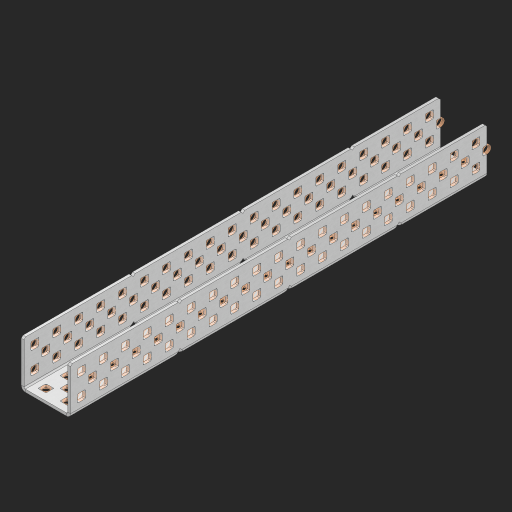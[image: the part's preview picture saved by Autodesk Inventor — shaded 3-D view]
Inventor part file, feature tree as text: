
AUTODESK INVENTOR PART (.ipt)
format: ipt  version: 2023 (Build 270158000, 158)  size: 2,187,264 bytes
history: native  units: in
note: dims shown in document units (in); Inventor stores cm internally (conversion verified against a paired STEP export)
features: other x234, extrude x226, sheet_metal_op x8, sketch x7, mirror x3, pattern_linear x2, chamfer x1
ambient origin geometry x8: Origin, YZ Plane, XZ Plane, XY Plane, X Axis, Y Axis, Z Axis, Center Point
bodies: Solid1 (feature_tree), Body (feature_tree)
feature tree (481):
  sheet_metal_op  "Flanges"
  sheet_metal_op  "Body Pattern"
  pattern_linear  "Center Pattern"  Spacing1=1.0in  [1 undecoded]
  other  "Arc Length"
  mirror  "Notch Mirror"
  pattern_linear  "Notch Pattern"  Spacing1=0.25in  [1 undecoded]
  other  "Diagonal Plane"
  mirror  "Flange 1"
  mirror  "Flange 2"
  chamfer  "End Chamfer"
  sketch  "Sketch1"  dims[d0=1.0in]
  other  "Plate1"
  sketch  "Sketch2"  dims[d1=9.5in]
  other  "Plate2"
  sheet_metal_op  "Bend1"
  sheet_metal_op  "Corner1"
  sketch  "Sketch8"  dims[d2=0.0625in]
  sketch  "Sketch9"  dims[d3=0.0625in]
  other  "Srf91"
  sheet_metal_op  "Body Pattern Sketch"
  other  "Srf92"
  sketch  "Sketch13"  dims[d4=0.0312in]
  sketch  "Sketch15"  dims[d5=0.125in]
  sketch  "Sketch16"  dims[d6=0.0625in d7=1.0in d8=90.0deg d9=0.0312in d10=0.25in d11=0.0625in d12=0.0625in d49=0.182in d50=0.02in d52=0.25in d53=0.0625in d54=0.0in d55=0.172in d56=1.0in d57=0.0in d60=7.4803in d62=0.5in d63=0.7874in d65=0.5in d85=0.1473in d86=0.1782in d88=0.04in d89=0.0625in d90=0.0in d91=0.04in d92=0.0491in d95=2.5in d96=0.04in d97=0.25in d98=45.0deg d99=0.25in d102=2.497in d106=0.182in d107=0.02in d108=0.5in d110=0.0625in d111=0.0in d112=0.172in d113=0.5in d114=0.0in d117=0.5in d118=0.5in d131=0.25in d132=0.25in]
  other  "Srf786"
  other  "Srf889"
  other  "Srf890"
  other  "Srf891"
  other  "Srf892"
  other  "Srf893"
  other  "Srf894"
  other  "Srf895"
  other  "Srf896"
  other  "Srf996"
  other  "Srf997"
  other  "Srf998"
  other  "Srf999"
  other  "Srf1000"
  other  "Srf1255"
  other  "Srf1256"
  other  "Srf1257"
  other  "Srf1258"
  other  "Srf1259"
  other  "Srf1315"
  other  "Srf1316"
  other  "Srf1317"
  other  "Srf1325"
  other  "Srf1326"
  other  "Srf1327"
  other  "Srf1328"
  other  "Srf1329"
  other  "Srf1330"
  other  "Srf1331"
  other  "Srf1332"
  other  "Srf1338"
  other  "Srf1339"
  other  "Srf1340"
  other  "Srf1341"
  other  "Srf1342"
  other  "Srf1369"
  other  "Srf1370"
  other  "Srf1371"
  other  "Srf1372"
  other  "Srf1373"
  other  "Srf1374"
  other  "Srf1375"
  other  "Srf1376"
  other  "Srf1384"
  other  "Srf1385"
  other  "Srf1386"
  other  "Srf1387"
  other  "Srf1388"
  other  "Srf1389"
  other  "Srf1390"
  other  "Srf1391"
  other  "Srf1397"
  other  "Srf1398"
  other  "Srf1399"
  other  "Srf1400"
  other  "Srf1401"
  other  "Srf1428"
  other  "Srf1429"
  other  "Srf1430"
  other  "Srf1431"
  other  "Srf1432"
  other  "Srf1433"
  other  "Srf1434"
  other  "Srf1473"
  other  "Srf1474"
  other  "Srf1475"
  other  "Srf1476"
  other  "Srf1477"
  other  "Srf1478"
  other  "Srf1479"
  other  "Srf1480"
  other  "Srf1481"
  other  "Srf1482"
  other  "Srf1483"
  other  "Srf1484"
  other  "Srf1485"
  other  "Srf1486"
  other  "Srf1487"
  other  "Srf1488"
  other  "Srf1489"
  other  "Srf1490"
  other  "Srf1491"
  other  "Srf1500"
  other  "Srf1501"
  other  "Srf1502"
  other  "Srf1503"
  other  "Srf1504"
  other  "Srf1505"
  other  "Srf1506"
  other  "Srf1507"
  other  "Srf1508"
  other  "Srf1509"
  other  "Srf1510"
  other  "Srf1511"
  other  "Srf1512"
  other  "Srf1513"
  other  "Srf1514"
  other  "Srf1515"
  other  "Srf1516"
  other  "Srf1517"
  other  "Srf1518"
  other  "Srf1519"
  other  "Srf1520"
  other  "Srf1521"
  other  "Srf1522"
  other  "Srf1523"
  other  "Srf1524"
  other  "Srf1525"
  other  "Srf1526"
  other  "Srf1527"
  other  "Srf1528"
  other  "Srf1529"
  other  "Srf1530"
  other  "Srf1531"
  other  "Srf1532"
  other  "Srf1533"
  other  "Srf1534"
  other  "Srf1535"
  other  "Srf1538"
  other  "Srf1539"
  other  "Srf1540"
  other  "Srf1541"
  other  "Srf1542"
  other  "Srf1543"
  other  "Srf1544"
  other  "Srf1545"
  other  "Srf1546"
  other  "Srf1547"
  other  "Srf1548"
  other  "Srf1549"
  other  "Srf1550"
  other  "Srf1551"
  other  "Srf1552"
  other  "Srf1553"
  other  "Srf1554"
  other  "Srf1555"
  other  "Srf1556"
  other  "Srf1557"
  other  "Srf1558"
  other  "Srf1559"
  other  "Srf1560"
  other  "Srf1561"
  other  "Srf1562"
  other  "Srf1563"
  other  "Srf1564"
  other  "Srf1565"
  other  "Srf1566"
  other  "Srf1567"
  other  "Srf1568"
  other  "Srf1569"
  other  "Srf1570"
  other  "Srf1571"
  other  "Srf1572"
  other  "Srf1573"
  other  "Srf1576"
  other  "Srf1577"
  other  "Srf1578"
  other  "Srf1579"
  other  "Srf1580"
  other  "Srf1581"
  other  "Srf1582"
  other  "Srf1583"
  other  "Srf1584"
  other  "Srf1585"
  other  "Srf1586"
  other  "Srf1587"
  other  "Srf1588"
  other  "Srf1589"
  other  "Srf1590"
  other  "Srf1591"
  other  "Srf1592"
  other  "Srf1593"
  other  "Srf1594"
  other  "Srf1595"
  other  "Srf1596"
  other  "Srf1597"
  other  "Srf1598"
  other  "Srf1599"
  other  "Srf1600"
  other  "Srf1601"
  other  "Srf1602"
  other  "Srf1603"
  other  "Srf1604"
  other  "Srf1605"
  other  "Srf1606"
  other  "Srf1607"
  other  "Srf1608"
  other  "Srf1609"
  other  "Srf1610"
  other  "Srf1611"
  other  "Srf1614"
  other  "Srf1615"
  other  "Srf1616"
  other  "Srf1617"
  other  "Srf1618"
  other  "Srf1619"
  other  "Srf1620"
  other  "Srf1621"
  other  "Srf1622"
  other  "Srf1623"
  other  "Srf1624"
  other  "Srf1625"
  other  "Srf1626"
  other  "Srf1627"
  other  "Srf1628"
  other  "Srf1629"
  other  "Srf1630"
  other  "Srf1631"
  other  "Srf1632"
  other  "Srf1633"
  other  "Srf1634"
  other  "Srf1635"
  other  "Srf1636"
  other  "Srf1637"
  other  "Srf1638"
  other  "Srf1639"
  other  "Srf1640"
  other  "Srf1641"
  other  "Srf1642"
  other  "Srf1643"
  other  "Srf1644"
  other  "Srf1645"
  other  "Srf1646"
  other  "Srf1647"
  other  "Srf1648"
  other  "Srf1649"
  sheet_metal_op  "Body Stamp"
  sheet_metal_op  "Body Circle"
  other  "Center Stamp"
  other  "Center Circle"
  sheet_metal_op  "Notch"
  extrude  "ExtrusionSrf92"  Depth=0.0625in
  extrude  "ExtrusionSrf889"  Depth=0.0625in
  extrude  "ExtrusionSrf890"  Depth=0.182in
  extrude  "ExtrusionSrf891"  Depth=0.02in
  extrude  "ExtrusionSrf892"  Depth=0.25in
  extrude  "ExtrusionSrf893"  Depth=0.0625in
  extrude  "ExtrusionSrf894"  TaperAngle=0.0deg  [1 undecoded]
  extrude  "ExtrusionSrf895"  Depth=0.25in
  extrude  "ExtrusionSrf896"  Depth=1.0in TaperAngle=0.0deg
  extrude  "ExtrusionSrf996"  Depth=0.25in
  extrude  "ExtrusionSrf997"  Depth=0.5in
  extrude  "ExtrusionSrf998"  Depth=0.25in
  extrude  "ExtrusionSrf999"  Depth=0.25in
  extrude  "ExtrusionSrf1000"  Depth=0.25in
  extrude  "ExtrusionSrf1255"  Depth=0.0625in
  extrude  "ExtrusionSrf1256"  TaperAngle=0.0deg  [1 undecoded]
  extrude  "ExtrusionSrf1257"  Depth=0.25in
  extrude  "ExtrusionSrf1258"  Depth=0.25in
  extrude  "ExtrusionSrf1259"  Depth=2.5in
  extrude  "ExtrusionSrf1315"  Depth=0.25in TaperAngle=45.0deg
  extrude  "ExtrusionSrf1316"  Depth=0.25in
  extrude  "ExtrusionSrf1355"  Depth=0.25in
  extrude  "ExtrusionSrf1356"  Depth=0.182in
  extrude  "ExtrusionSrf1357"  Depth=0.02in
  extrude  "ExtrusionSrf1358"  Depth=0.5in
  extrude  "ExtrusionSrf1359"  Depth=0.0625in
  extrude  "ExtrusionSrf1360"  TaperAngle=0.0deg  [1 undecoded]
  extrude  "ExtrusionSrf1361"  Depth=0.25in
  extrude  "ExtrusionSrf1362"  Depth=0.5in TaperAngle=0.0deg
  extrude  "ExtrusionSrf1363"  Depth=0.5in
  extrude  "ExtrusionSrf1364"  Depth=0.5in
  extrude  "ExtrusionSrf1365"  Depth=0.25in
  extrude  "ExtrusionSrf1366"  Depth=0.25in
  extrude  "ExtrusionSrf1367"  [1 undecoded]
  extrude  "ExtrusionSrf1368"  [1 undecoded]
  extrude  "ExtrusionSrf1369"  [1 undecoded]
  extrude  "ExtrusionSrf1370"  [1 undecoded]
  extrude  "ExtrusionSrf1371"  [1 undecoded]
  extrude  "ExtrusionSrf1372"  [1 undecoded]
  extrude  "ExtrusionSrf1373"  [1 undecoded]
  extrude  "ExtrusionSrf1374"  [1 undecoded]
  extrude  "ExtrusionSrf1375"  [1 undecoded]
  extrude  "ExtrusionSrf1414"  [1 undecoded]
  extrude  "ExtrusionSrf1415"  [1 undecoded]
  extrude  "ExtrusionSrf1416"  [1 undecoded]
  extrude  "ExtrusionSrf1417"  [1 undecoded]
  extrude  "ExtrusionSrf1418"  [1 undecoded]
  extrude  "ExtrusionSrf1419"  [1 undecoded]
  extrude  "ExtrusionSrf1420"  [1 undecoded]
  extrude  "ExtrusionSrf1421"  [1 undecoded]
  extrude  "ExtrusionSrf1422"  [1 undecoded]
  extrude  "ExtrusionSrf1423"  [1 undecoded]
  extrude  "ExtrusionSrf1424"  [1 undecoded]
  extrude  "ExtrusionSrf1425"  [1 undecoded]
  extrude  "ExtrusionSrf1426"  [1 undecoded]
  extrude  "ExtrusionSrf1427"  [1 undecoded]
  extrude  "ExtrusionSrf1428"  [1 undecoded]
  extrude  "ExtrusionSrf1429"  [1 undecoded]
  extrude  "ExtrusionSrf1430"  [1 undecoded]
  extrude  "ExtrusionSrf1431"  [1 undecoded]
  extrude  "ExtrusionSrf1432"  [1 undecoded]
  extrude  "ExtrusionSrf1433"  [1 undecoded]
  extrude  "ExtrusionSrf1434"  [1 undecoded]
  extrude  "ExtrusionSrf1473"  [1 undecoded]
  extrude  "ExtrusionSrf1474"  [1 undecoded]
  extrude  "ExtrusionSrf1475"  [1 undecoded]
  extrude  "ExtrusionSrf1476"  [1 undecoded]
  extrude  "ExtrusionSrf1477"  [1 undecoded]
  extrude  "ExtrusionSrf1478"  [1 undecoded]
  extrude  "ExtrusionSrf1479"  [1 undecoded]
  extrude  "ExtrusionSrf1480"  [1 undecoded]
  extrude  "ExtrusionSrf1481"  [1 undecoded]
  extrude  "ExtrusionSrf1482"  [1 undecoded]
  extrude  "ExtrusionSrf1483"  [1 undecoded]
  extrude  "ExtrusionSrf1484"  [1 undecoded]
  extrude  "ExtrusionSrf1485"  [1 undecoded]
  extrude  "ExtrusionSrf1486"  [1 undecoded]
  extrude  "ExtrusionSrf1487"  [1 undecoded]
  extrude  "ExtrusionSrf1488"  [1 undecoded]
  extrude  "ExtrusionSrf1489"  [1 undecoded]
  extrude  "ExtrusionSrf1490"  [1 undecoded]
  extrude  "ExtrusionSrf1491"  [1 undecoded]
  extrude  "ExtrusionSrf1500"  [1 undecoded]
  extrude  "ExtrusionSrf1501"  [1 undecoded]
  extrude  "ExtrusionSrf1502"  [1 undecoded]
  extrude  "ExtrusionSrf1503"  [1 undecoded]
  extrude  "ExtrusionSrf1504"  [1 undecoded]
  extrude  "ExtrusionSrf1505"  [1 undecoded]
  extrude  "ExtrusionSrf1506"  [1 undecoded]
  extrude  "ExtrusionSrf1507"  [1 undecoded]
  extrude  "ExtrusionSrf1508"  [1 undecoded]
  extrude  "ExtrusionSrf1509"  [1 undecoded]
  extrude  "ExtrusionSrf1510"  [1 undecoded]
  extrude  "ExtrusionSrf1511"  [1 undecoded]
  extrude  "ExtrusionSrf1512"  [1 undecoded]
  extrude  "ExtrusionSrf1513"  [1 undecoded]
  extrude  "ExtrusionSrf1514"  [1 undecoded]
  extrude  "ExtrusionSrf1515"  [1 undecoded]
  extrude  "ExtrusionSrf1516"  [1 undecoded]
  extrude  "ExtrusionSrf1517"  [1 undecoded]
  extrude  "ExtrusionSrf1518"  [1 undecoded]
  extrude  "ExtrusionSrf1519"  [1 undecoded]
  extrude  "ExtrusionSrf1520"  [1 undecoded]
  extrude  "ExtrusionSrf1521"  [1 undecoded]
  extrude  "ExtrusionSrf1522"  [1 undecoded]
  extrude  "ExtrusionSrf1523"  [1 undecoded]
  extrude  "ExtrusionSrf1524"  [1 undecoded]
  extrude  "ExtrusionSrf1525"  [1 undecoded]
  extrude  "ExtrusionSrf1526"  [1 undecoded]
  extrude  "ExtrusionSrf1527"  [1 undecoded]
  extrude  "ExtrusionSrf1528"  [1 undecoded]
  extrude  "ExtrusionSrf1529"  [1 undecoded]
  extrude  "ExtrusionSrf1530"  [1 undecoded]
  extrude  "ExtrusionSrf1531"  [1 undecoded]
  extrude  "ExtrusionSrf1532"  [1 undecoded]
  extrude  "ExtrusionSrf1533"  [1 undecoded]
  extrude  "ExtrusionSrf1534"  [1 undecoded]
  extrude  "ExtrusionSrf1535"  [1 undecoded]
  extrude  "ExtrusionSrf1538"  [1 undecoded]
  extrude  "ExtrusionSrf1539"  [1 undecoded]
  extrude  "ExtrusionSrf1540"  [1 undecoded]
  extrude  "ExtrusionSrf1541"  [1 undecoded]
  extrude  "ExtrusionSrf1542"  [1 undecoded]
  extrude  "ExtrusionSrf1543"  [1 undecoded]
  extrude  "ExtrusionSrf1544"  [1 undecoded]
  extrude  "ExtrusionSrf1545"  [1 undecoded]
  extrude  "ExtrusionSrf1546"  [1 undecoded]
  extrude  "ExtrusionSrf1547"  [1 undecoded]
  extrude  "ExtrusionSrf1548"  [1 undecoded]
  extrude  "ExtrusionSrf1549"  [1 undecoded]
  extrude  "ExtrusionSrf1550"  [1 undecoded]
  extrude  "ExtrusionSrf1551"  [1 undecoded]
  extrude  "ExtrusionSrf1552"  [1 undecoded]
  extrude  "ExtrusionSrf1553"  [1 undecoded]
  extrude  "ExtrusionSrf1554"  [1 undecoded]
  extrude  "ExtrusionSrf1555"  [1 undecoded]
  extrude  "ExtrusionSrf1556"  [1 undecoded]
  extrude  "ExtrusionSrf1557"  [1 undecoded]
  extrude  "ExtrusionSrf1558"  [1 undecoded]
  extrude  "ExtrusionSrf1559"  [1 undecoded]
  extrude  "ExtrusionSrf1560"  [1 undecoded]
  extrude  "ExtrusionSrf1561"  [1 undecoded]
  extrude  "ExtrusionSrf1562"  [1 undecoded]
  extrude  "ExtrusionSrf1563"  [1 undecoded]
  extrude  "ExtrusionSrf1564"  [1 undecoded]
  extrude  "ExtrusionSrf1565"  [1 undecoded]
  extrude  "ExtrusionSrf1566"  [1 undecoded]
  extrude  "ExtrusionSrf1567"  [1 undecoded]
  extrude  "ExtrusionSrf1568"  [1 undecoded]
  extrude  "ExtrusionSrf1569"  [1 undecoded]
  extrude  "ExtrusionSrf1570"  [1 undecoded]
  extrude  "ExtrusionSrf1571"  [1 undecoded]
  extrude  "ExtrusionSrf1572"  [1 undecoded]
  extrude  "ExtrusionSrf1573"  [1 undecoded]
  extrude  "ExtrusionSrf1576"  [1 undecoded]
  extrude  "ExtrusionSrf1577"  [1 undecoded]
  extrude  "ExtrusionSrf1578"  [1 undecoded]
  extrude  "ExtrusionSrf1579"  [1 undecoded]
  extrude  "ExtrusionSrf1580"  [1 undecoded]
  extrude  "ExtrusionSrf1581"  [1 undecoded]
  extrude  "ExtrusionSrf1582"  [1 undecoded]
  extrude  "ExtrusionSrf1583"  [1 undecoded]
  extrude  "ExtrusionSrf1584"  [1 undecoded]
  extrude  "ExtrusionSrf1585"  [1 undecoded]
  extrude  "ExtrusionSrf1586"  [1 undecoded]
  extrude  "ExtrusionSrf1587"  [1 undecoded]
  extrude  "ExtrusionSrf1588"  [1 undecoded]
  extrude  "ExtrusionSrf1589"  [1 undecoded]
  extrude  "ExtrusionSrf1590"  [1 undecoded]
  extrude  "ExtrusionSrf1591"  [1 undecoded]
  extrude  "ExtrusionSrf1592"  [1 undecoded]
  extrude  "ExtrusionSrf1593"  [1 undecoded]
  extrude  "ExtrusionSrf1594"  [1 undecoded]
  extrude  "ExtrusionSrf1595"  [1 undecoded]
  extrude  "ExtrusionSrf1596"  [1 undecoded]
  extrude  "ExtrusionSrf1597"  [1 undecoded]
  extrude  "ExtrusionSrf1598"  [1 undecoded]
  extrude  "ExtrusionSrf1599"  [1 undecoded]
  extrude  "ExtrusionSrf1600"  [1 undecoded]
  extrude  "ExtrusionSrf1601"  [1 undecoded]
  extrude  "ExtrusionSrf1602"  [1 undecoded]
  extrude  "ExtrusionSrf1603"  [1 undecoded]
  extrude  "ExtrusionSrf1604"  [1 undecoded]
  extrude  "ExtrusionSrf1605"  [1 undecoded]
  extrude  "ExtrusionSrf1606"  [1 undecoded]
  extrude  "ExtrusionSrf1607"  [1 undecoded]
  extrude  "ExtrusionSrf1608"  [1 undecoded]
  extrude  "ExtrusionSrf1609"  [1 undecoded]
  extrude  "ExtrusionSrf1610"  [1 undecoded]
  extrude  "ExtrusionSrf1611"  [1 undecoded]
  extrude  "ExtrusionSrf1614"  [1 undecoded]
  extrude  "ExtrusionSrf1615"  [1 undecoded]
  extrude  "ExtrusionSrf1616"  [1 undecoded]
  extrude  "ExtrusionSrf1617"  [1 undecoded]
  extrude  "ExtrusionSrf1618"  [1 undecoded]
  extrude  "ExtrusionSrf1619"  [1 undecoded]
  extrude  "ExtrusionSrf1620"  [1 undecoded]
  extrude  "ExtrusionSrf1621"  [1 undecoded]
  extrude  "ExtrusionSrf1622"  [1 undecoded]
  extrude  "ExtrusionSrf1623"  [1 undecoded]
  extrude  "ExtrusionSrf1624"  [1 undecoded]
  extrude  "ExtrusionSrf1625"  [1 undecoded]
  extrude  "ExtrusionSrf1626"  [1 undecoded]
  extrude  "ExtrusionSrf1627"  [1 undecoded]
  extrude  "ExtrusionSrf1628"  [1 undecoded]
  extrude  "ExtrusionSrf1629"  [1 undecoded]
  extrude  "ExtrusionSrf1630"  [1 undecoded]
  extrude  "ExtrusionSrf1631"  [1 undecoded]
  extrude  "ExtrusionSrf1632"  [1 undecoded]
  extrude  "ExtrusionSrf1633"  [1 undecoded]
  extrude  "ExtrusionSrf1634"  [1 undecoded]
  extrude  "ExtrusionSrf1635"  [1 undecoded]
  extrude  "ExtrusionSrf1636"  [1 undecoded]
  extrude  "ExtrusionSrf1637"  [1 undecoded]
  extrude  "ExtrusionSrf1638"  [1 undecoded]
  extrude  "ExtrusionSrf1639"  [1 undecoded]
  extrude  "ExtrusionSrf1640"  [1 undecoded]
  extrude  "ExtrusionSrf1641"  [1 undecoded]
  extrude  "ExtrusionSrf1642"  [1 undecoded]
  extrude  "ExtrusionSrf1643"  [1 undecoded]
  extrude  "ExtrusionSrf1644"  [1 undecoded]
  extrude  "ExtrusionSrf1645"  [1 undecoded]
  extrude  "ExtrusionSrf1646"  [1 undecoded]
  extrude  "ExtrusionSrf1647"  [1 undecoded]
  extrude  "ExtrusionSrf1648"  [1 undecoded]
  extrude  "ExtrusionSrf1649"  [1 undecoded]
note: 198 required parameter values undecoded (feature->parameter linkage not recoverable at this tier; creation-order binding heuristic only, values carry confidence <= 0.55)
